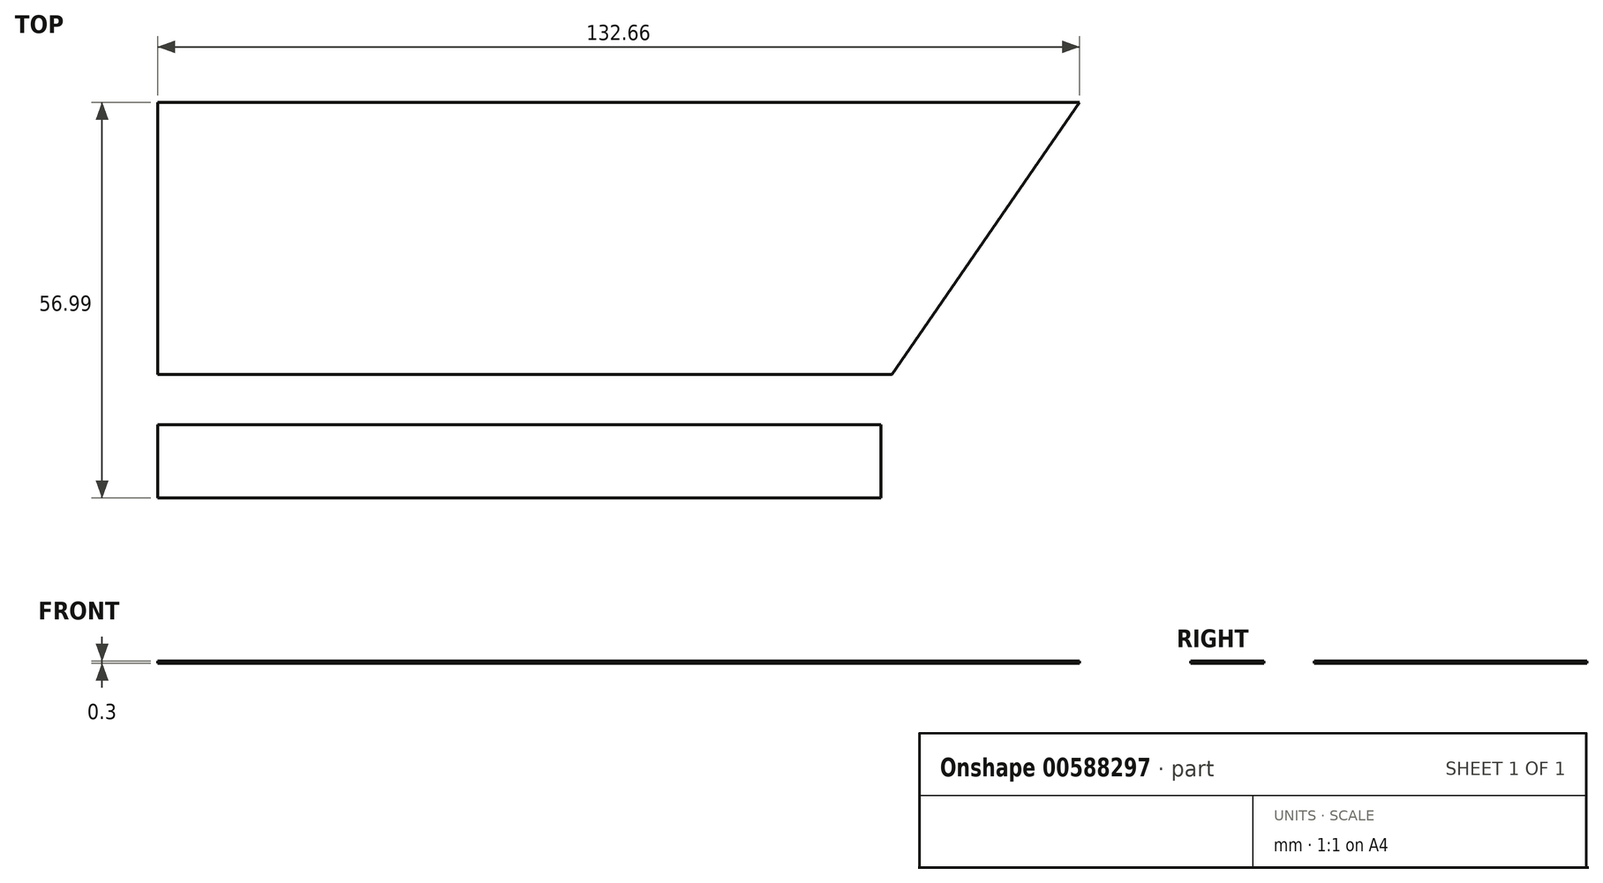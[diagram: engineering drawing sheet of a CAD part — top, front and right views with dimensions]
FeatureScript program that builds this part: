
annotation { "Feature Type Name" : "Feature", "Feature Type Description" : "" }
export const myFeature = defineFeature(function(context is Context, id is Id, definition is map)
    precondition{}
    {
        {
            var Q0;
            Q0=qCreatedBy(makeId("Top.planeOp"),FACE);
            var sketch = newSketch(context, id + "F0", { "sketchPlane" : qUnion([Q0])});
            skLineSegment(sketch, "E0.bottom", {"start": v(-69.1, 2.35) * mm, "end": v(33.55, 2.35) * mm});
            skLineSegment(sketch, "E0.top", {"start": v(-69.1, -8.18) * mm, "end": v(33.55, -8.18) * mm});
            skLineSegment(sketch, "E0.left", {"start": v(-69.1, 2.35) * mm, "end": v(-69.1, -8.18) * mm});
            skLineSegment(sketch, "E1", {"start": v(33.55, 2.35) * mm, "end": v(33.95, 2.35) * mm});
            skLineSegment(sketch, "E2", {"start": v(33.95, -8.18) * mm, "end": v(33.55, -8.18) * mm});
            skLineSegment(sketch, "E3", {"start": v(-69.1, -8.18) * mm, "end": v(-69.1, 9.6) * mm});
            skLineSegment(sketch, "E4", {"start": v(-69.1, 9.6) * mm, "end": v(36.55, 9.6) * mm});
            skLineSegment(sketch, "E5", {"start": v(-69.1, 9.6) * mm, "end": v(-69.1, 48.81) * mm});
            skLineSegment(sketch, "E6", {"start": v(-69.1, 48.81) * mm, "end": v(54.34, 48.81) * mm});
            skLineSegment(sketch, "E7", {"start": v(54.34, 48.81) * mm, "end": v(63.56, 48.81) * mm});
            skLineSegment(sketch, "E8", {"start": v(63.56, 48.81) * mm, "end": v(36.55, 9.6) * mm});
            skPoint(sketch, "E9.orphan", {"position": v(63.56, 59.41) * mm});
            skLineSegment(sketch, "E10", {"start": v(33.95, 2.35) * mm, "end": v(34.95, 2.35) * mm});
            skLineSegment(sketch, "E11", {"start": v(34.95, 2.35) * mm, "end": v(34.95, -8.18) * mm});
            skLineSegment(sketch, "E12", {"start": v(34.95, -8.18) * mm, "end": v(33.95, -8.18) * mm});
            skSolve(sketch);
        }
        {
            var Q0;
            Q0=makeQuery(id+"F0.imprint","IMPRINT",FACE,{"disambiguationData":[TD([[makeQuery(id+"F0.imprint","IMPRINT",EDGE,{"derivedFrom":sQuery(id+"F0.wireOp",EDGE,"E0.bottom")}),-1.0]])]});
            extrude(context, id + "F1", {"entities" : qUnion([Q0]), "depth" : .3 * mm, "offsetDistance" : 25 * mm});
        }
        {
            var Q0;
            Q0=makeQuery(id+"F0.imprint","IMPRINT",FACE,{"disambiguationData":[TD([[makeQuery(id+"F0.imprint","IMPRINT",EDGE,{"derivedFrom":sQuery(id+"F0.wireOp",EDGE,"E4")}),1.0]])]});
            extrude(context, id + "F2", {"entities" : qUnion([Q0]), "depth" : .3 * mm, "offsetDistance" : 25 * mm});
        }
    });
